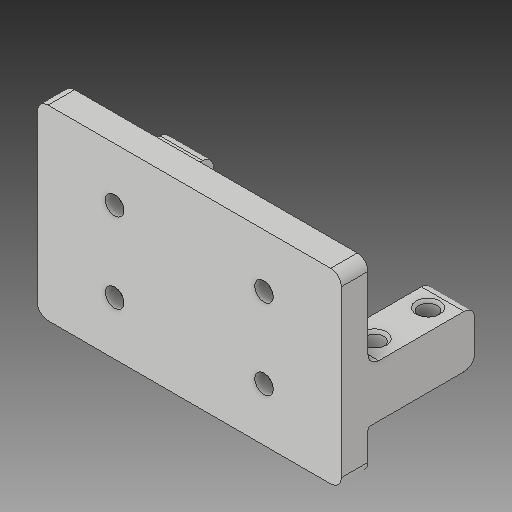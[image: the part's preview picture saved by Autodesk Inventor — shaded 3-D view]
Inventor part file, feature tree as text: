
AUTODESK INVENTOR PART (.ipt)
format: ipt  version: 2019 (Build 230136000, 136)  size: 192,000 bytes
history: native  units: mm
features: sketch x4, other x3
ambient origin geometry x8: Origin, YZ Plane, XZ Plane, XY Plane, X Axis, Y Axis, Z Axis, Center Point
bodies: Solid1 (feature_tree)
feature tree (7):
  other  "big_servo_hold.ipt"
  other  "Solid1::big_servo_hold.ipt"
  other  "TaggingFeature1"
  sketch  "Sketch1"  dims[d0=10.0mm]
  sketch  "Sketch2"
  sketch  "Sketch4"
  sketch  "Sketch5"
